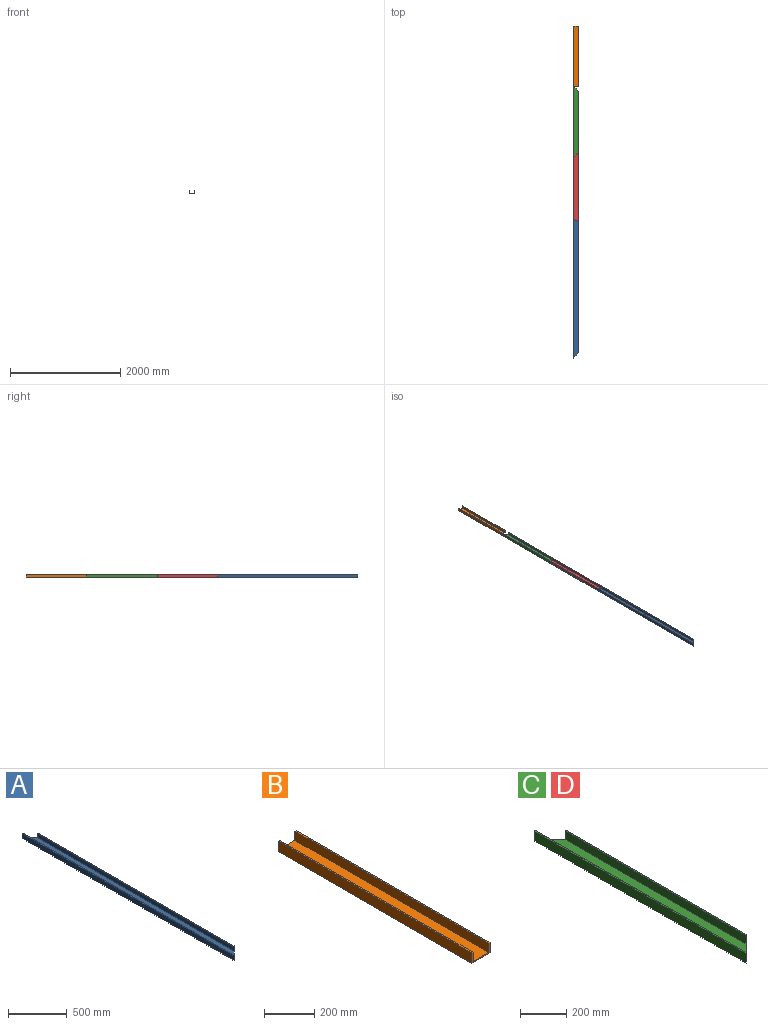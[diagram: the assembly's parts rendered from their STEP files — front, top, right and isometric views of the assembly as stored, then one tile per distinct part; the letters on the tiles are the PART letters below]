
ASSEMBLY  parts=4 mates=3
PART A: 10 faces, bbox 101.6x2543.2x50.8 mm
  f0: plane 2530.48x88.9mm, normal (0,0,1), area 217056mm2, adj f1,f3,f6,f8
  f1: plane 101.6x101.6mm, normal (0.71,-0.71,0), area 1710.7mm2, adj f0,f2,f4,f5,f6,f7,f8,f9
  f2: plane 2339.98x50.8mm, normal (1,0,0), area 118870.7mm2, adj f1,f3,f5,f7
  f3: plane 101.6x101.6mm, normal (0.71,0.71,0), area 1710.7mm2, adj f0,f2,f4,f5,f6,f7,f8,f9
  f4: plane 2543.18x50.8mm, normal (-1,0,0), area 129193.3mm2, adj f1,f3,f5,f9
  f5: plane 2543.18x101.6mm, normal (0,0,-1), area 248064mm2, adj f1,f2,f3,f4
  f6: plane 2352.68x44.45mm, normal (-1,0,0), area 104576.4mm2, adj f0,f1,f3,f7
  f7: plane 2352.68x6.35mm, normal (0,0,1), area 14899.2mm2, adj f1,f2,f3,f6
  f8: plane 2530.48x44.45mm, normal (1,0,0), area 112479.6mm2, adj f0,f1,f3,f9
  f9: plane 2543.18x6.35mm, normal (0,0,1), area 16108.8mm2, adj f1,f3,f4,f8
PART B: 10 faces, bbox 101.6x1090.6x50.8 mm
  f0: plane 1090.62x88.9mm, normal (0,0,1), area 96956.1mm2, adj f1,f3,f6,f8
  f1: plane 101.6x50.8mm, normal (0,-1,0), area 1209.7mm2, adj f0,f2,f4,f5,f6,f7,f8,f9
  f2: plane 1090.62x50.8mm, normal (1,0,0), area 55403.2mm2, adj f1,f3,f5,f7
  f3: plane 101.6x50.8mm, normal (0,1,0), area 1209.7mm2, adj f0,f2,f4,f5,f6,f7,f8,f9
  f4: plane 1090.63x50.8mm, normal (-1,0,0), area 55403.8mm2, adj f1,f3,f5,f9
  f5: plane 1090.63x101.6mm, normal (0,0,-1), area 110807mm2, adj f1,f2,f3,f4
  f6: plane 1090.62x44.45mm, normal (-1,0,0), area 48477.9mm2, adj f0,f1,f3,f7
  f7: plane 1090.62x6.35mm, normal (0,0,1), area 6925.4mm2, adj f1,f2,f3,f6
  f8: plane 1090.62x44.45mm, normal (1,0,0), area 48478.3mm2, adj f0,f1,f3,f9
  f9: plane 1090.63x6.35mm, normal (0,0,1), area 6925.5mm2, adj f1,f3,f4,f8
PART C: 10 faces, bbox 101.6x1293.8x50.8 mm
  f0: plane 1281.12x88.9mm, normal (0,0,1), area 105987.9mm2, adj f1,f3,f6,f8
  f1: plane 101.6x101.6mm, normal (0.71,-0.71,0), area 1710.7mm2, adj f0,f2,f4,f5,f6,f7,f8,f9
  f2: plane 1090.62x50.8mm, normal (1,0,0), area 55403.2mm2, adj f1,f3,f5,f7
  f3: plane 101.6x101.6mm, normal (0.71,0.71,0), area 1710.7mm2, adj f0,f2,f4,f5,f6,f7,f8,f9
  f4: plane 1293.82x50.8mm, normal (-1,0,0), area 65725.8mm2, adj f1,f3,f5,f9
  f5: plane 1293.82x101.6mm, normal (0,0,-1), area 121129mm2, adj f1,f2,f3,f4
  f6: plane 1103.32x44.45mm, normal (-1,0,0), area 49042.4mm2, adj f0,f1,f3,f7
  f7: plane 1103.32x6.35mm, normal (0,0,1), area 6965.7mm2, adj f1,f2,f3,f6
  f8: plane 1281.12x44.45mm, normal (1,0,0), area 56945.6mm2, adj f0,f1,f3,f9
  f9: plane 1293.82x6.35mm, normal (0,0,1), area 8175.4mm2, adj f1,f3,f4,f8
PART D: same geometry as C
PLACE A t=(-265.81,-115.46,28.52)mm
PLACE B t=(-265.81,4084.08,28.83)mm
PLACE C t=(-265.81,2891.86,28.83)mm
PLACE D rot(axis=(0,0,-1),180deg) t=(-266.07,1701.69,28.55)mm
MATE planar D.f3 <-> A.f3  axis (-0.71,-0.71,0) through (-266.07,1105.59,34.9)mm
MATE fastened B.f9 <-> C.f9  axis (0,0,1) through (-316.61,3538.77,79.63)mm
MATE planar D.f1 <-> D.f5  axis (-0.71,0.71,0) through (-266.07,2297.8,43.58)mm
